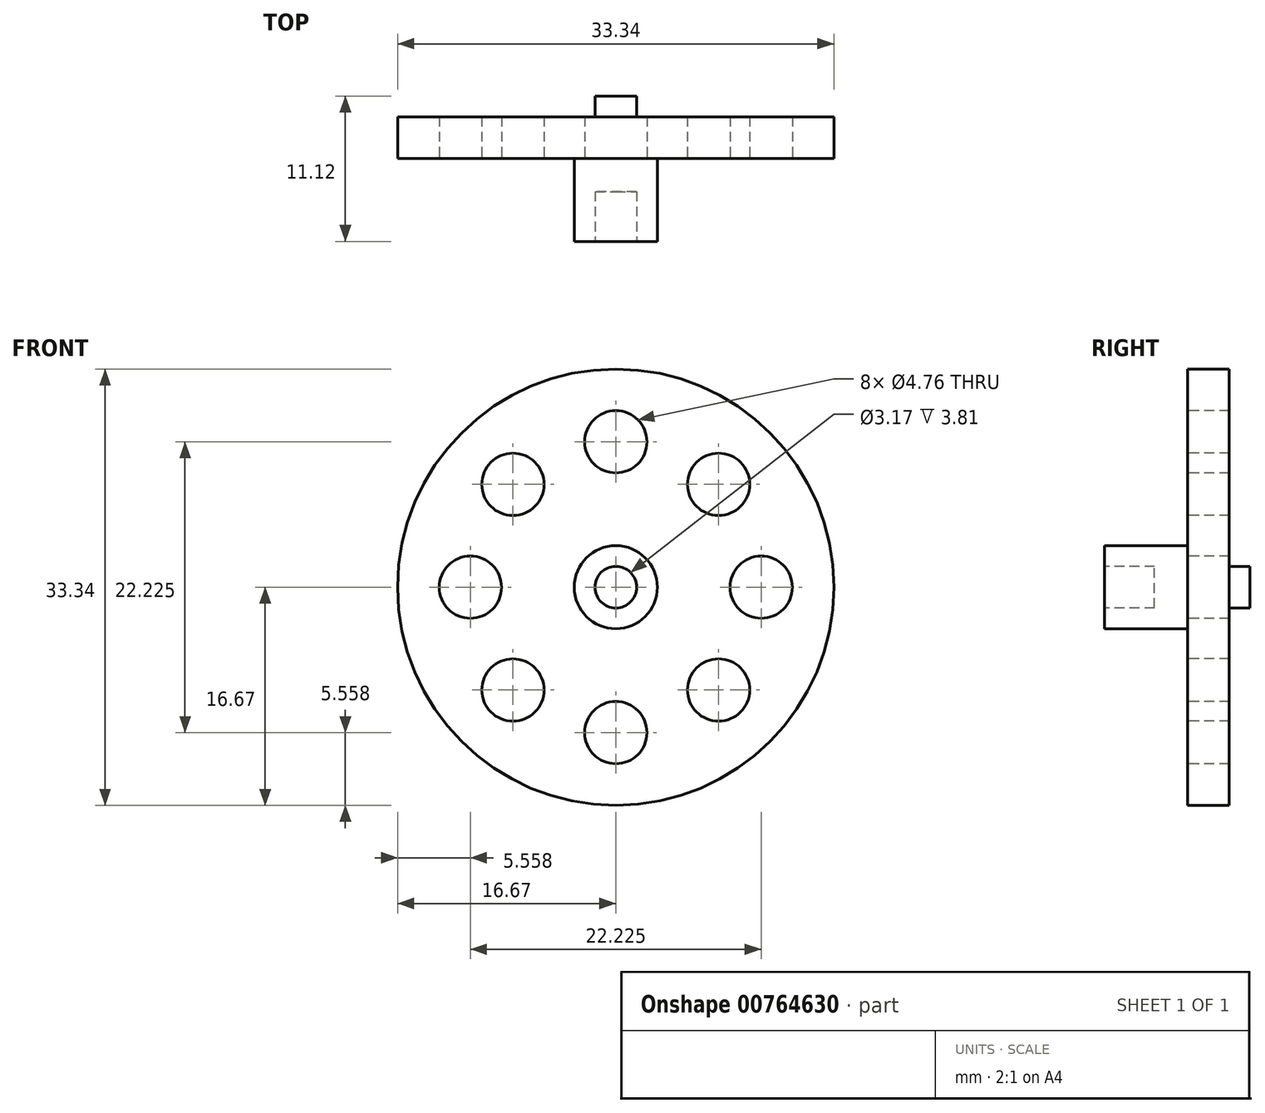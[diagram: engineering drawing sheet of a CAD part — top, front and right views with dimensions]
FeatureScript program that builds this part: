
annotation { "Feature Type Name" : "Feature", "Feature Type Description" : "" }
export const myFeature = defineFeature(function(context is Context, id is Id, definition is map)
    precondition{}
    {
        {
            var Q0;
            Q0=qCreatedBy(makeId("Front.planeOp"),FACE);
            var sketch = newSketch(context, id + "F0", { "sketchPlane" : qUnion([Q0])});
            skCircle(sketch, "E0", {"center": v(0, 0) * mm, "radius": 16.67 * mm});
            skSolve(sketch);
        }
        {
            var Q0;
            Q0=makeQuery(id+"F0.imprint","IMPRINT",FACE,{"disambiguationData":[TD([[makeQuery(id+"F0.imprint","IMPRINT",EDGE,{"derivedFrom":sQuery(id+"F0.wireOp",EDGE,"E0")}),1.0]])]});
            extrude(context, id + "F1", {"entities" : qUnion([Q0]), "depth" : 3.17 * mm, "offsetDistance" : 25.4 * mm});
        }
        {
            var Q0;
            Q0=makeQuery(id+"F1.opExtrude","CAP_FACE",FACE,{"disambiguationData":[OSD([sQuery(id+"F0.wireOp",EDGE,"E0")])],"isStart":false});
            var sketch = newSketch(context, id + "F2", { "sketchPlane" : qUnion([Q0])});
            skCircle(sketch, "E1", {"center": v(0, 0) * mm, "radius": 3.18 * mm});
            skSolve(sketch);
        }
        {
            var Q0;
            Q0=makeQuery(id+"F2.imprint","IMPRINT",FACE,{"disambiguationData":[TD([[makeQuery(id+"F2.imprint","IMPRINT",EDGE,{"derivedFrom":sQuery(id+"F2.wireOp",EDGE,"E1")}),1.0]])]});
            extrude(context, id + "F3", {"entities" : qUnion([Q0]), "operationType" : NewBodyOperationType.ADD, "depth" : 6.35 * mm, "offsetDistance" : 25.4 * mm});
        }
        {
            var Q0;
            Q0=makeQuery(id+"F3.opExtrude","CAP_FACE",FACE,{"disambiguationData":[OSD([sQuery(id+"F2.wireOp",EDGE,"E1")])],"isStart":false});
            var sketch = newSketch(context, id + "F4", { "sketchPlane" : qUnion([Q0])});
            skCircle(sketch, "E2", {"center": v(0, 0) * mm, "radius": 1.59 * mm});
            skSolve(sketch);
        }
        {
            var Q0;
            Q0=makeQuery(id+"F4.imprint","IMPRINT",FACE,{"disambiguationData":[TD([[makeQuery(id+"F4.imprint","IMPRINT",EDGE,{"derivedFrom":sQuery(id+"F4.wireOp",EDGE,"E2")}),1.0]])]});
            extrude(context, id + "F5", {"entities" : qUnion([Q0]), "operationType" : NewBodyOperationType.REMOVE, "oppositeDirection" : true, "depth" : 3.8 * mm, "offsetDistance" : 25.4 * mm});
        }
        {
            var Q0;
            Q0=makeQuery(id+"F1.opExtrude","CAP_FACE",FACE,{"disambiguationData":[OSD([sQuery(id+"F0.wireOp",EDGE,"E0")])],"isStart":false});
            var sketch = newSketch(context, id + "F6", { "sketchPlane" : qUnion([Q0])});
            skCircle(sketch, "E3", {"center": v(11.11, 0) * mm, "radius": 2.38 * mm});
            skCircle(sketch, "E4.1.0", {"center": v(7.86, 7.86) * mm, "radius": 2.38 * mm});
            skCircle(sketch, "E4.2.0", {"center": v(0, 11.11) * mm, "radius": 2.38 * mm});
            skCircle(sketch, "E4.3.0", {"center": v(-7.86, 7.86) * mm, "radius": 2.38 * mm});
            skCircle(sketch, "E4.4.0", {"center": v(-11.11, 0) * mm, "radius": 2.38 * mm});
            skCircle(sketch, "E4.5.0", {"center": v(-7.86, -7.86) * mm, "radius": 2.38 * mm});
            skCircle(sketch, "E4.6.0", {"center": v(0, -11.11) * mm, "radius": 2.38 * mm});
            skCircle(sketch, "E4.7.0", {"center": v(7.86, -7.86) * mm, "radius": 2.38 * mm});
            skPoint(sketch, "E4.center", {"position": v(0, 0) * mm});
            skSolve(sketch);
        }
        {
            var Q0;
            Q0 = qSketchRegion(id + "F6", true);
            extrude(context, id + "F7", {"entities" : qUnion([Q0]), "operationType" : NewBodyOperationType.REMOVE, "oppositeDirection" : true, "depth" : 25.4 * mm, "offsetDistance" : 25.4 * mm});
        }
        {
            var Q0;
            Q0=makeQuery(id+"F1.opExtrude","CAP_FACE",FACE,{"disambiguationData":[OSD([sQuery(id+"F0.wireOp",EDGE,"E0")])],"isStart":true});
            var sketch = newSketch(context, id + "F8", { "sketchPlane" : qUnion([Q0])});
            skCircle(sketch, "E5", {"center": v(0, 0) * mm, "radius": 1.59 * mm});
            skSolve(sketch);
        }
        {
            var Q0;
            Q0=makeQuery(id+"F8.imprint","IMPRINT",FACE,{"disambiguationData":[TD([[makeQuery(id+"F8.imprint","IMPRINT",EDGE,{"derivedFrom":sQuery(id+"F8.wireOp",EDGE,"E5")}),1.0]])]});
            extrude(context, id + "F9", {"entities" : qUnion([Q0]), "operationType" : NewBodyOperationType.ADD, "depth" : 1.59 * mm, "offsetDistance" : 25.4 * mm});
        }
    });
